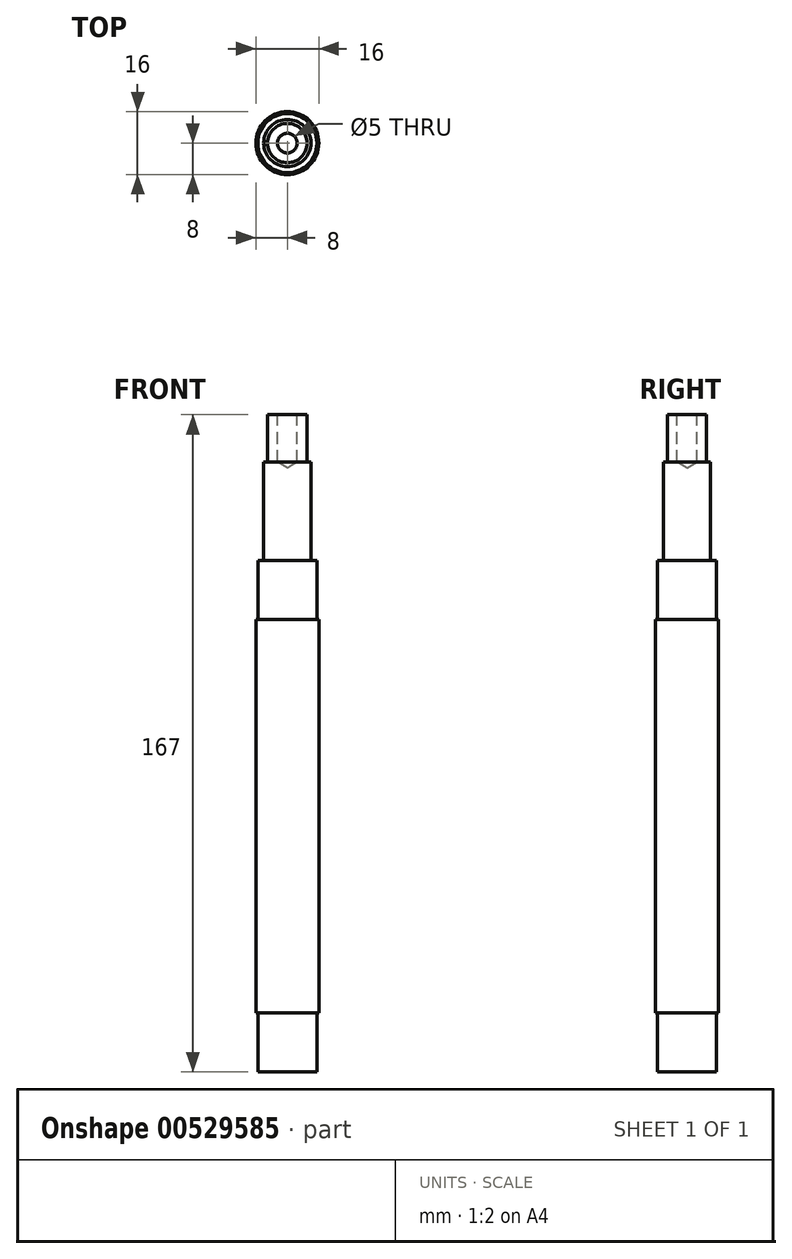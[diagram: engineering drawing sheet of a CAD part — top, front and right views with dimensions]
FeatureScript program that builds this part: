
annotation { "Feature Type Name" : "Feature", "Feature Type Description" : "" }
export const myFeature = defineFeature(function(context is Context, id is Id, definition is map)
    precondition{}
    {
        {
            var Q0;
            Q0=qCreatedBy(makeId("Top.planeOp"),FACE);
            var sketch = newSketch(context, id + "F0", { "sketchPlane" : qUnion([Q0])});
            skCircle(sketch, "E0", {"center": v(0, 0) * mm, "radius": 7.5 * mm});
            skSolve(sketch);
        }
        {
            var Q0;
            Q0 = qSketchRegion(id + "F0", true);
            extrude(context, id + "F1", {"entities" : qUnion([Q0]), "depth" : 15 * mm, "offsetDistance" : 25 * mm});
        }
        {
            var Q0;
            Q0=makeQuery(id+"F1.opExtrude","CAP_FACE",FACE,{"disambiguationData":[OSD([sQuery(id+"F0.wireOp",EDGE,"E0")])],"isStart":false});
            var sketch = newSketch(context, id + "F2", { "sketchPlane" : qUnion([Q0])});
            skCircle(sketch, "E1", {"center": v(0, 0) * mm, "radius": 8 * mm});
            skSolve(sketch);
        }
        {
            var Q0;
            Q0 = qSketchRegion(id + "F2", true);
            extrude(context, id + "F3", {"entities" : qUnion([Q0]), "operationType" : NewBodyOperationType.ADD, "depth" : 100 * mm, "offsetDistance" : 25 * mm});
        }
        {
            var Q0;
            Q0=makeQuery(id+"F3.opExtrude","CAP_FACE",FACE,{"disambiguationData":[OSD([sQuery(id+"F2.wireOp",EDGE,"E1")])],"isStart":false});
            var sketch = newSketch(context, id + "F4", { "sketchPlane" : qUnion([Q0])});
            skCircle(sketch, "E2", {"center": v(0, 0) * mm, "radius": 7.5 * mm});
            skSolve(sketch);
        }
        {
            var Q0;
            Q0 = qSketchRegion(id + "F4", true);
            extrude(context, id + "F5", {"entities" : qUnion([Q0]), "operationType" : NewBodyOperationType.ADD, "depth" : 15 * mm, "offsetDistance" : 25 * mm});
        }
        {
            var Q0;
            Q0=makeQuery(id+"F5.opExtrude","CAP_FACE",FACE,{"disambiguationData":[OSD([sQuery(id+"F4.wireOp",EDGE,"E2")])],"isStart":false});
            var sketch = newSketch(context, id + "F6", { "sketchPlane" : qUnion([Q0])});
            skCircle(sketch, "E3", {"center": v(0, 0) * mm, "radius": 6 * mm});
            skSolve(sketch);
        }
        {
            var Q0;
            Q0=makeQuery(id+"F6.imprint","IMPRINT",FACE,{"disambiguationData":[TD([[makeQuery(id+"F6.imprint","IMPRINT",EDGE,{"derivedFrom":sQuery(id+"F6.wireOp",EDGE,"E3")}),1.0]])]});
            extrude(context, id + "F7", {"entities" : qUnion([Q0]), "operationType" : NewBodyOperationType.ADD, "depth" : 25 * mm, "offsetDistance" : 25 * mm});
        }
        {
            var Q0;
            Q0=makeQuery(id+"F7.opExtrude","CAP_FACE",FACE,{"disambiguationData":[OSD([sQuery(id+"F6.wireOp",EDGE,"E3")])],"isStart":false});
            var sketch = newSketch(context, id + "F8", { "sketchPlane" : qUnion([Q0])});
            skCircle(sketch, "E4", {"center": v(0, 0) * mm, "radius": 5 * mm});
            skSolve(sketch);
        }
        {
            var Q0;
            Q0 = qSketchRegion(id + "F8", true);
            extrude(context, id + "F9", {"entities" : qUnion([Q0]), "operationType" : NewBodyOperationType.ADD, "depth" : 12 * mm, "offsetDistance" : 25 * mm});
        }
        {
            var Q0;
            Q0=makeQuery(id+"F9.opExtrude","CAP_FACE",FACE,{"disambiguationData":[OSD([sQuery(id+"F8.wireOp",EDGE,"E4")])],"isStart":false});
            var sketch = newSketch(context, id + "F10", { "sketchPlane" : qUnion([Q0])});
            skPoint(sketch, "E5", {"position": v(0, 0) * mm});
            skSolve(sketch);
        }
        {
            var Q0;
            Q0=sQuery(id+"F10.wireOp",VERTEX,"E5");
            var Q1;
            Q1=makeQuery(id+"F1.opExtrude","SWEPT_BODY",BODY,{"disambiguationData":[OSD([sQuery(id+"F0.wireOp",EDGE,"E0")])]});
            hole(context, id + "F11", {"style" : HoleStyle.SIMPLE, "endStyle" : HoleEndStyle.BLIND, "standardTappedOrClearance" : lookupTablePath({ "standard" : "ISO", "engagement" : "75%", "pitch" : "1 mm", "size" : "M6", "type" : "Tapped" }), "standardBlindInLast" : lookupTablePath({ "standard" : "ISO", "engagement" : "75%", "pitch" : "1 mm", "size" : "M6", "type" : "Tapped" }), "holeDiameter" : 5 * mm, "showTappedDepth" : true, "holeDepth" : 12 * mm, "isTappedThrough" : true, "tappedDepth" : 9 * mm, "tapClearance" : 3, "locations" : qUnion([Q0]), "scope" : qUnion([Q1]), "majorDiameter" : 6 * mm});
        }
    });
